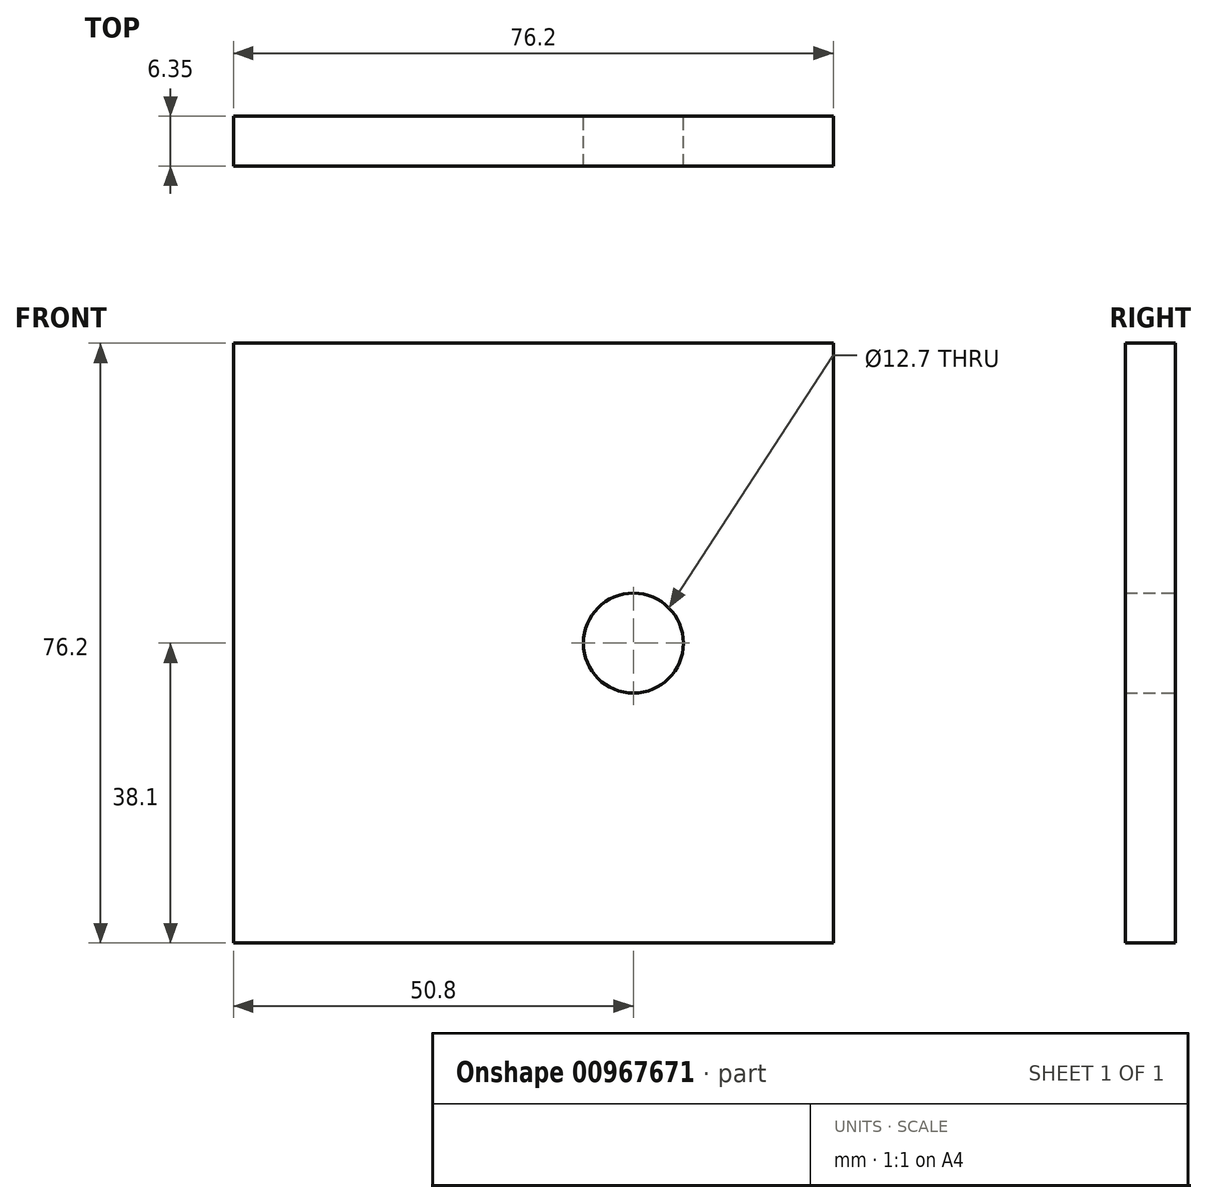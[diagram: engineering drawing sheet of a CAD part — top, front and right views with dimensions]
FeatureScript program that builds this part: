
annotation { "Feature Type Name" : "Feature", "Feature Type Description" : "" }
export const myFeature = defineFeature(function(context is Context, id is Id, definition is map)
    precondition{}
    {
        {
            var Q0;
            Q0=qCreatedBy(makeId("Front.planeOp"),FACE);
            var sketch = newSketch(context, id + "F0", { "sketchPlane" : qUnion([Q0])});
            skCircle(sketch, "E0", {"center": v(0, 0) * mm, "radius": 6.35 * mm});
            skLineSegment(sketch, "E1.bottom", {"start": v(-50.8, -38.1) * mm, "end": v(25.4, -38.1) * mm});
            skLineSegment(sketch, "E1.top", {"start": v(-50.8, 38.1) * mm, "end": v(25.4, 38.1) * mm});
            skLineSegment(sketch, "E1.left", {"start": v(-50.8, -38.1) * mm, "end": v(-50.8, 38.1) * mm});
            skLineSegment(sketch, "E1.right", {"start": v(25.4, -38.1) * mm, "end": v(25.4, 38.1) * mm});
            skSolve(sketch);
        }
        {
            var Q0;
            Q0 = qSketchRegion(id + "F0", true);
            extrude(context, id + "F1", {"entities" : qUnion([Q0]), "depth" : 6.35 * mm, "offsetDistance" : 25.4 * mm});
        }
    });
